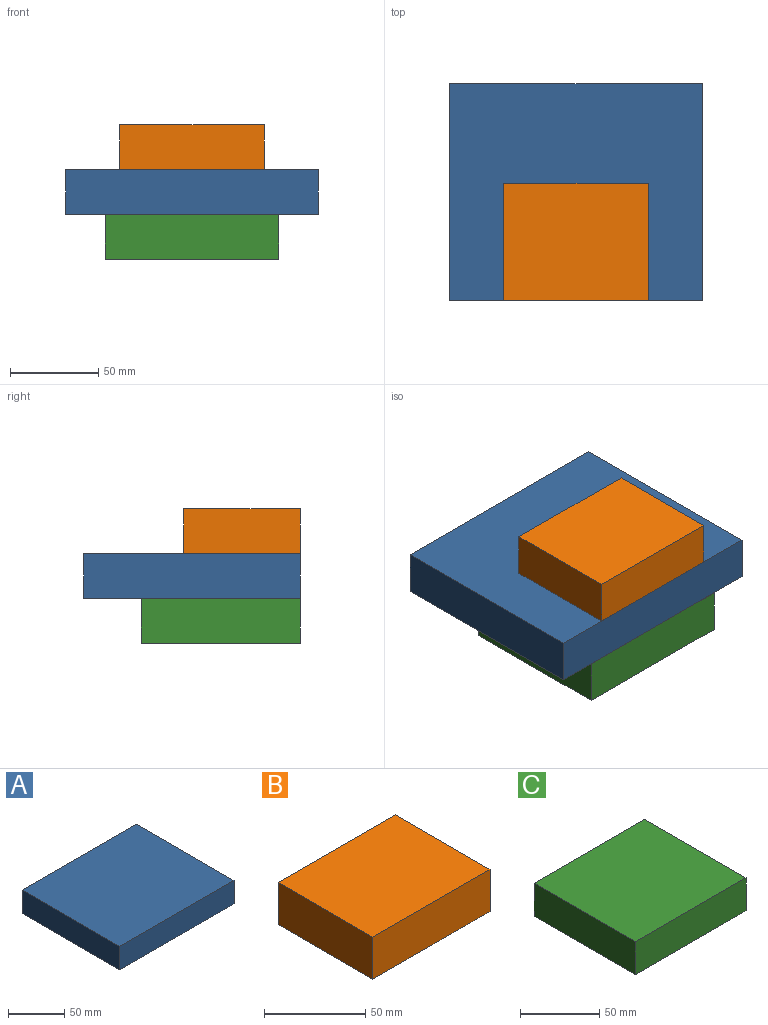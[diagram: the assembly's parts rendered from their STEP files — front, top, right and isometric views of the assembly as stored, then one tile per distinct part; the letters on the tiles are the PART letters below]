
ASSEMBLY  parts=3 mates=2
PART A: 6 faces, bbox 143.1x122.7x25.4 mm
  f0: plane 143.11x25.4mm, normal (0,1,0), area 3635.1mm2, adj f1,f3,f4,f5
  f1: plane 122.7x25.4mm, normal (-1,0,0), area 3116.5mm2, adj f0,f2,f4,f5
  f2: plane 143.11x25.4mm, normal (0,-1,0), area 3635.1mm2, adj f1,f3,f4,f5
  f3: plane 122.7x25.4mm, normal (1,0,0), area 3116.5mm2, adj f0,f2,f4,f5
  f4: plane 143.11x122.7mm, normal (0,0,1), area 17559.9mm2, adj f0,f1,f2,f3
  f5: plane 143.11x122.7mm, normal (0,0,-1), area 17559.9mm2, adj f0,f1,f2,f3
PART B: 6 faces, bbox 81.7x66.2x25.4 mm
  f0: plane 81.72x25.4mm, normal (0,1,0), area 2075.8mm2, adj f1,f3,f4,f5
  f1: plane 66.16x25.4mm, normal (-1,0,0), area 1680.4mm2, adj f0,f2,f4,f5
  f2: plane 81.72x25.4mm, normal (0,-1,0), area 2075.8mm2, adj f1,f3,f4,f5
  f3: plane 66.16x25.4mm, normal (1,0,0), area 1680.4mm2, adj f0,f2,f4,f5
  f4: plane 81.72x66.16mm, normal (0,0,1), area 5406.6mm2, adj f0,f1,f2,f3
  f5: plane 81.72x66.16mm, normal (0,0,-1), area 5406.6mm2, adj f0,f1,f2,f3
PART C: 6 faces, bbox 98.5x90.2x25.4 mm
  f0: plane 98.46x25.4mm, normal (0,1,0), area 2500.9mm2, adj f1,f3,f4,f5
  f1: plane 90.17x25.4mm, normal (-1,0,0), area 2290.2mm2, adj f0,f2,f4,f5
  f2: plane 98.46x25.4mm, normal (0,-1,0), area 2500.9mm2, adj f1,f3,f4,f5
  f3: plane 90.17x25.4mm, normal (1,0,0), area 2290.2mm2, adj f0,f2,f4,f5
  f4: plane 98.46x90.17mm, normal (0,0,1), area 8877.9mm2, adj f0,f1,f2,f3
  f5: plane 98.46x90.17mm, normal (0,0,-1), area 8877.9mm2, adj f0,f1,f2,f3
PLACE A t=(6.42,273.32,141.15)mm
PLACE B t=(-100.03,38.22,166.55)mm
PLACE C t=(148.63,64.44,115.75)mm
MATE fastened A.f4 <-> B.f5  axis (0,0,1) through (20.18,80.91,166.55)mm
MATE fastened C.f4 <-> A.f5  axis (0,0,1) through (20.18,80.91,141.15)mm
